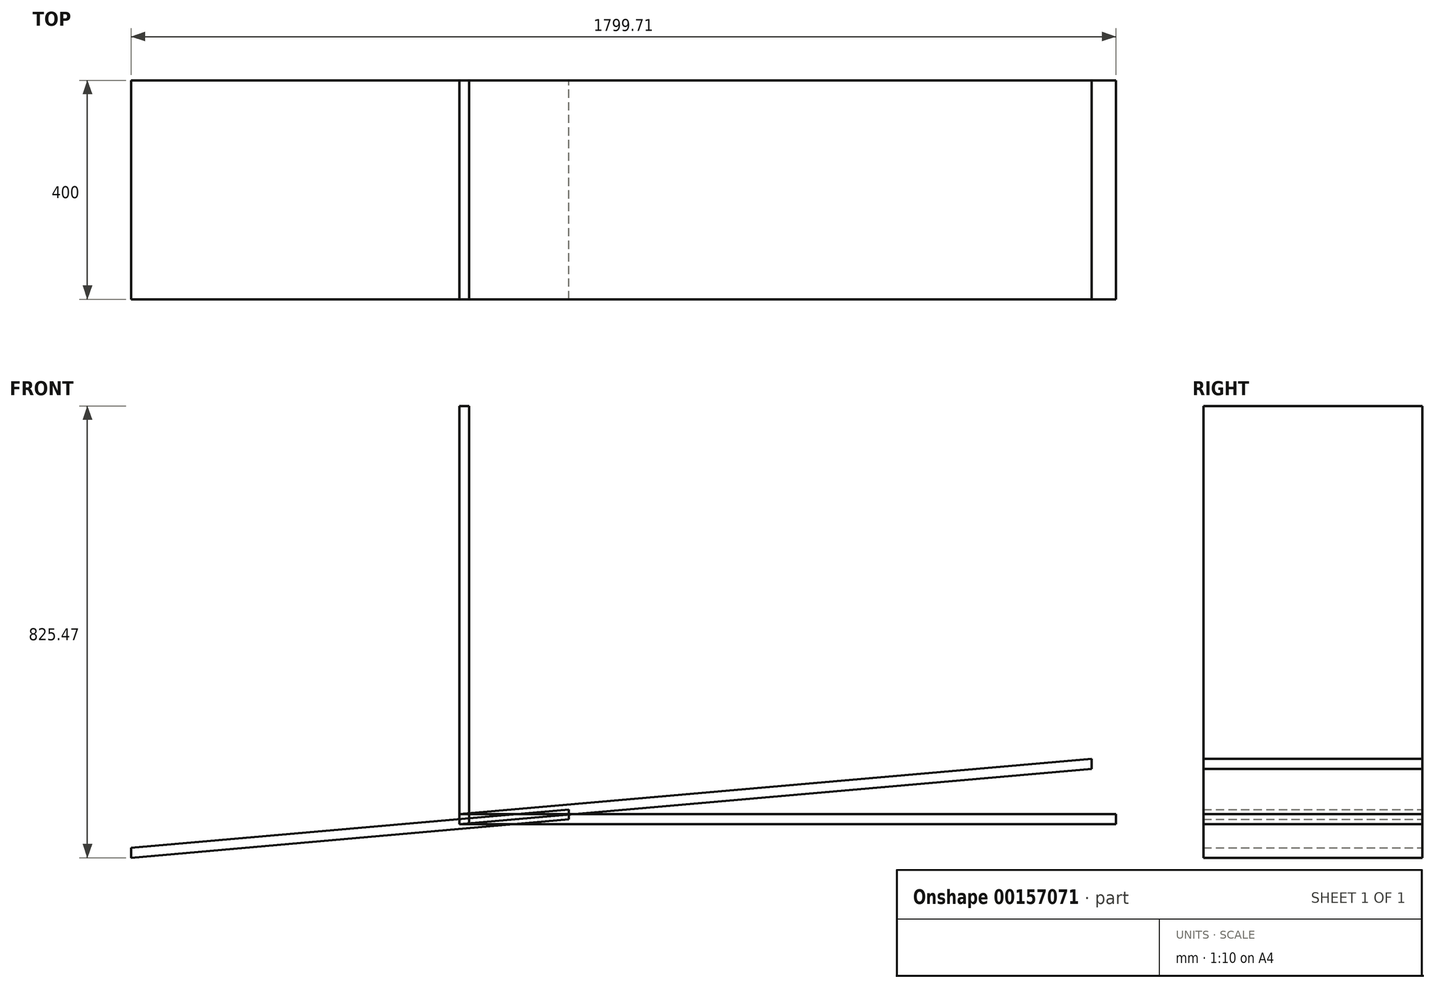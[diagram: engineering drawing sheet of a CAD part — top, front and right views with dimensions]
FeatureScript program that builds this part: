
annotation { "Feature Type Name" : "Feature", "Feature Type Description" : "" }
export const myFeature = defineFeature(function(context is Context, id is Id, definition is map)
    precondition{}
    {
        {
            var Q0;
            Q0=qCreatedBy(makeId("Top.planeOp"),FACE);
            var sketch = newSketch(context, id + "F0", { "sketchPlane" : qUnion([Q0])});
            skLineSegment(sketch, "E0.bottom", {"start": v(0, 0) * mm, "end": v(18, 0) * mm});
            skLineSegment(sketch, "E0.top", {"start": v(0, -400) * mm, "end": v(18, -400) * mm});
            skLineSegment(sketch, "E0.left", {"start": v(0, 0) * mm, "end": v(0, -400) * mm});
            skLineSegment(sketch, "E0.right", {"start": v(18, 0) * mm, "end": v(18, -400) * mm});
            skSolve(sketch);
        }
        {
            var Q0;
            Q0 = qSketchRegion(id + "F0", true);
            extrude(context, id + "F1", {"entities" : qUnion([Q0]), "depth" : 764 * mm});
        }
        {
            var Q0;
            Q0=qCreatedBy(makeId("Front.planeOp"),FACE);
            var sketch = newSketch(context, id + "F2", { "sketchPlane" : qUnion([Q0])});
            skLineSegment(sketch, "E1.bottom", {"start": v(0, 0) * mm, "end": v(1155.59, 101.1) * mm});
            skLineSegment(sketch, "E1.top", {"start": v(0, 18) * mm, "end": v(1155.59, 119.1) * mm});
            skLineSegment(sketch, "E1.left", {"start": v(0, 0) * mm, "end": v(0, 18) * mm});
            skLineSegment(sketch, "E1.right", {"start": v(1155.59, 101.1) * mm, "end": v(1155.59, 119.1) * mm});
            skSolve(sketch);
        }
        {
            var Q0;
            Q0 = qSketchRegion(id + "F2", true);
            extrude(context, id + "F3", {"entities" : qUnion([Q0]), "depth" : 400 * mm});
        }
        {
            var Q0;
            Q0=qCreatedBy(makeId("Right.planeOp"),FACE);
            var sketch = newSketch(context, id + "F4", { "sketchPlane" : qUnion([Q0])});
            skLineSegment(sketch, "E2.bottom", {"start": v(0, 0) * mm, "end": v(-400, 0) * mm});
            skLineSegment(sketch, "E2.top", {"start": v(0, 18) * mm, "end": v(-400, 18) * mm});
            skLineSegment(sketch, "E2.left", {"start": v(0, 0) * mm, "end": v(0, 18) * mm});
            skLineSegment(sketch, "E2.right", {"start": v(-400, 0) * mm, "end": v(-400, 18) * mm});
            skSolve(sketch);
        }
        {
            var Q0;
            Q0 = qSketchRegion(id + "F4", true);
            extrude(context, id + "F5", {"entities" : qUnion([Q0]), "depth" : 1200 * mm});
        }
        {
            var Q0;
            Q0=qCreatedBy(makeId("Front.planeOp"),FACE);
            var sketch = newSketch(context, id + "F6", { "sketchPlane" : qUnion([Q0])});
            skLineSegment(sketch, "E3.bottom", {"start": v(-599.7, -61.47) * mm, "end": v(200.24, 8.52) * mm});
            skLineSegment(sketch, "E3.top", {"start": v(-599.7, -43.47) * mm, "end": v(200.24, 26.52) * mm});
            skLineSegment(sketch, "E3.left", {"start": v(-599.7, -61.47) * mm, "end": v(-599.7, -43.47) * mm});
            skLineSegment(sketch, "E3.right", {"start": v(200.24, 8.52) * mm, "end": v(200.24, 26.52) * mm});
            skSolve(sketch);
        }
        {
            var Q0;
            Q0 = qSketchRegion(id + "F6", true);
            extrude(context, id + "F7", {"entities" : qUnion([Q0]), "depth" : 400 * mm});
        }
    });
